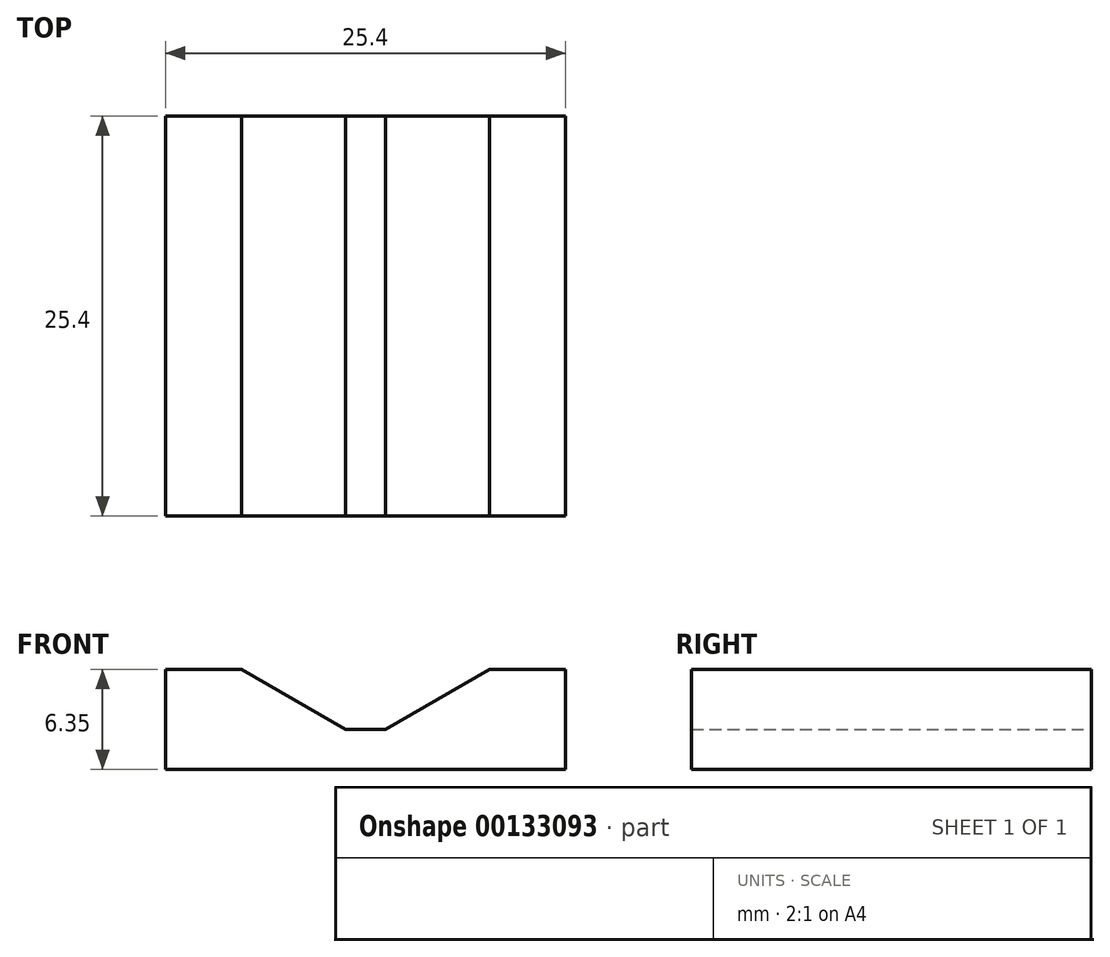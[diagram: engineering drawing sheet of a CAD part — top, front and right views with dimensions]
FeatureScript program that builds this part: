
annotation { "Feature Type Name" : "Feature", "Feature Type Description" : "" }
export const myFeature = defineFeature(function(context is Context, id is Id, definition is map)
    precondition{}
    {
        {
            var Q0;
            Q0=qCreatedBy(makeId("Front.planeOp"),FACE);
            var sketch = newSketch(context, id + "F0", { "sketchPlane" : qUnion([Q0])});
            skLineSegment(sketch, "E0", {"start": v(0, 0) * mm, "end": v(0, 5.56) * mm, "construction": true});
            skLineSegment(sketch, "E1", {"start": v(-12.7, 6.35) * mm, "end": v(-7.87, 6.35) * mm});
            skLineSegment(sketch, "E2", {"start": v(12.7, 6.35) * mm, "end": v(12.7, 0) * mm});
            skLineSegment(sketch, "E3", {"start": v(12.7, 0) * mm, "end": v(-12.7, 0) * mm});
            skLineSegment(sketch, "E4", {"start": v(-12.7, 0) * mm, "end": v(-12.7, 6.35) * mm});
            skLineSegment(sketch, "E5", {"start": v(-7.87, 6.35) * mm, "end": v(-1.27, 2.54) * mm});
            skLineSegment(sketch, "E6.trimOffspring", {"start": v(7.87, 6.35) * mm, "end": v(12.7, 6.35) * mm});
            skLineSegment(sketch, "E7", {"start": v(-1.27, 2.54) * mm, "end": v(1.27, 2.54) * mm});
            skLineSegment(sketch, "E8", {"start": v(1.27, 2.54) * mm, "end": v(7.87, 6.35) * mm});
            skSolve(sketch);
        }
        {
            var Q0;
            Q0 = qSketchRegion(id + "F0", true);
            extrude(context, id + "F1", {"entities" : qUnion([Q0]), "depth" : 25.4 * mm});
        }
    });
